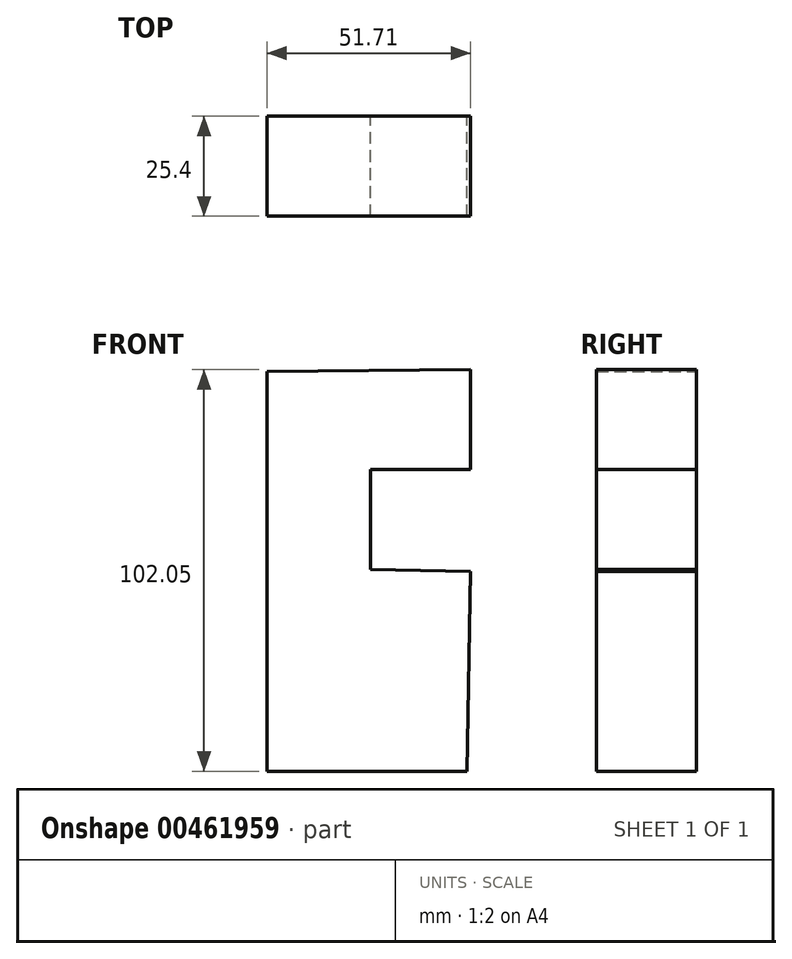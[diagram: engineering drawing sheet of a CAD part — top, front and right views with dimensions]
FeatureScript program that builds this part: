
annotation { "Feature Type Name" : "Feature", "Feature Type Description" : "" }
export const myFeature = defineFeature(function(context is Context, id is Id, definition is map)
    precondition{}
    {
        {
            var Q0;
            Q0=qCreatedBy(makeId("Front.planeOp"),FACE);
            var sketch = newSketch(context, id + "F0", { "sketchPlane" : qUnion([Q0])});
            skLineSegment(sketch, "E0", {"start": v(-51.7, 94.41) * mm, "end": v(-51.7, -7.19) * mm});
            skLineSegment(sketch, "E1", {"start": v(-51.7, -7.19) * mm, "end": v(-0.9, -7.19) * mm});
            skLineSegment(sketch, "E2", {"start": v(-0.9, -7.19) * mm, "end": v(0, 43.6) * mm});
            skLineSegment(sketch, "E3", {"start": v(0, 43.6) * mm, "end": v(-25.4, 44.06) * mm});
            skLineSegment(sketch, "E4", {"start": v(-25.4, 44.06) * mm, "end": v(-25.4, 69.46) * mm});
            skLineSegment(sketch, "E5", {"start": v(-25.4, 69.46) * mm, "end": v(0, 69.46) * mm});
            skLineSegment(sketch, "E6", {"start": v(0, 69.46) * mm, "end": v(0, 94.86) * mm});
            skLineSegment(sketch, "E7", {"start": v(0, 94.86) * mm, "end": v(-51.7, 94.41) * mm});
            skSolve(sketch);
        }
        {
            var Q0;
            Q0=makeQuery(id+"F0.imprint","IMPRINT",FACE,{"disambiguationData":[TD([[makeQuery(id+"F0.imprint","IMPRINT",EDGE,{"derivedFrom":sQuery(id+"F0.wireOp",EDGE,"E0")}),1.0]])]});
            extrude(context, id + "F1", {"entities" : qUnion([Q0]), "depth" : 25.4 * mm});
        }
    });
